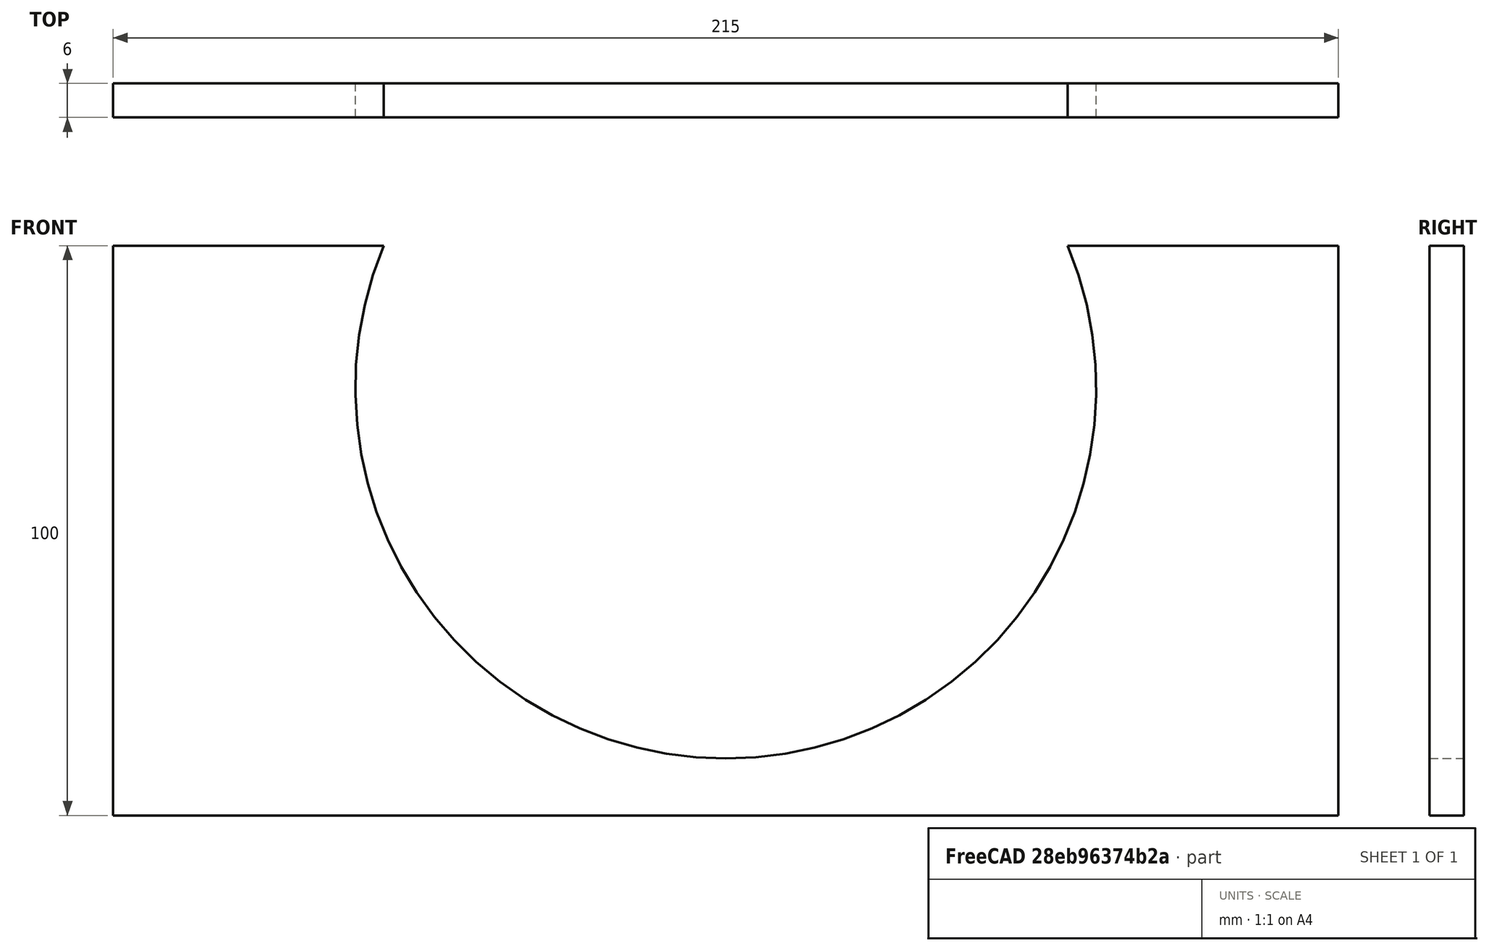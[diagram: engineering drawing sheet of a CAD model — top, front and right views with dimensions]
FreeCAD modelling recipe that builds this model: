
FCSTD DOCUMENT  (FreeCAD 0.18R4 (GitTag))
Label: soporte1
License: All rights reserved
LicenseURL: http://en.wikipedia.org/wiki/All_rights_reserved
objects: Sketcher::SketchObject×1, PartDesign::Pad×1, PartDesign::Body×1
note: 4 computed .brp shape members not serialized (recipe doc carries the construction recipe); baked Part::Feature solids carry a one-line shape summary decoded from their .brp

FEATURE [Sketcher::SketchObject] Sketch
  MapMode = 5
  Placement = pos=(0,0,0) rot=(1,0,0;1.5708rad)
  Support = -> [XZ_Plane]
  sketch-geometry (6):
    g0: LineSegment StartX=0 StartY=0 StartZ=0 EndX=215 EndY=0 EndZ=0
    g1: LineSegment StartX=215 StartY=0 StartZ=0 EndX=215 EndY=100 EndZ=0
    g2: LineSegment StartX=215 StartY=100 StartZ=0 EndX=167.5 EndY=100 EndZ=0
    g3: LineSegment StartX=0 StartY=100 StartZ=0 EndX=0 EndY=0 EndZ=0
    g4: ArcOfCircle CenterX=107.5 CenterY=75 CenterZ=0 NormalX=0 NormalY=0 NormalZ=1 AngleXU=0 Radius=65 StartAngle=2.7468 EndAngle=6.67798
    g5: LineSegment StartX=47.5 StartY=100 StartZ=0 EndX=0 EndY=100 EndZ=0
  constraints (17):
    c: Coincident(g0,g1)
    c: Coincident(g1,g2)
    c: Coincident(g3,g0)
    c: Horizontal(g0)
    c: Horizontal(g2)
    c: Vertical(g1)
    c: Vertical(g3)
    c: DistanceX(g0,g0) = 215
    c: DistanceY(g3,g3) = 100
    c: Coincident(g0,g-1)
    c: Radius(g4) = 65
    c: Coincident(g5,g4)
    c: Tangent(g2,g5)
    c: Coincident(g2,g4)
    c: Distance(g4,g3) = 107.5
    c: Distance(g4,g0) = 75
    c: Coincident(g3,g5)
FEATURE [PartDesign::Pad] Pad
  Length = 6
  Length2 = 100
  Placement = pos=(0,0,0) rot=(1,0,0;1.5708rad)
  Profile = -> Sketch
  Type = 0
FEATURE [PartDesign::Body] Body
  Group = -> [Sketch,Pad]
  Origin = -> Origin
  Tip = -> Pad
